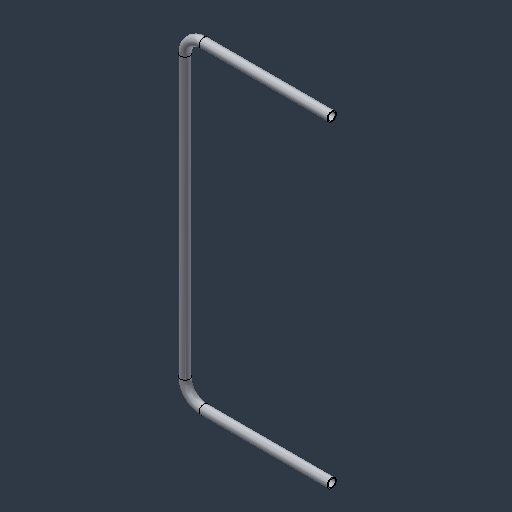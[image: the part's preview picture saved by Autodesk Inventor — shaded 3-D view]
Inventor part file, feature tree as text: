
AUTODESK INVENTOR PART (.ipt)
format: ipt  version: 2024.3 (Build 283343000, 343)  size: 99,328 bytes
history: native  units: mm (DEFAULTED — no unit token found)
features: sweep x1
ambient origin geometry x8: Origin, YZ Plane, XZ Plane, XY Plane, X Axis, Y Axis, Z Axis, Center Point
bodies: Solid1 (feature_tree)
feature tree (1):
  sweep  "Sweep1"
